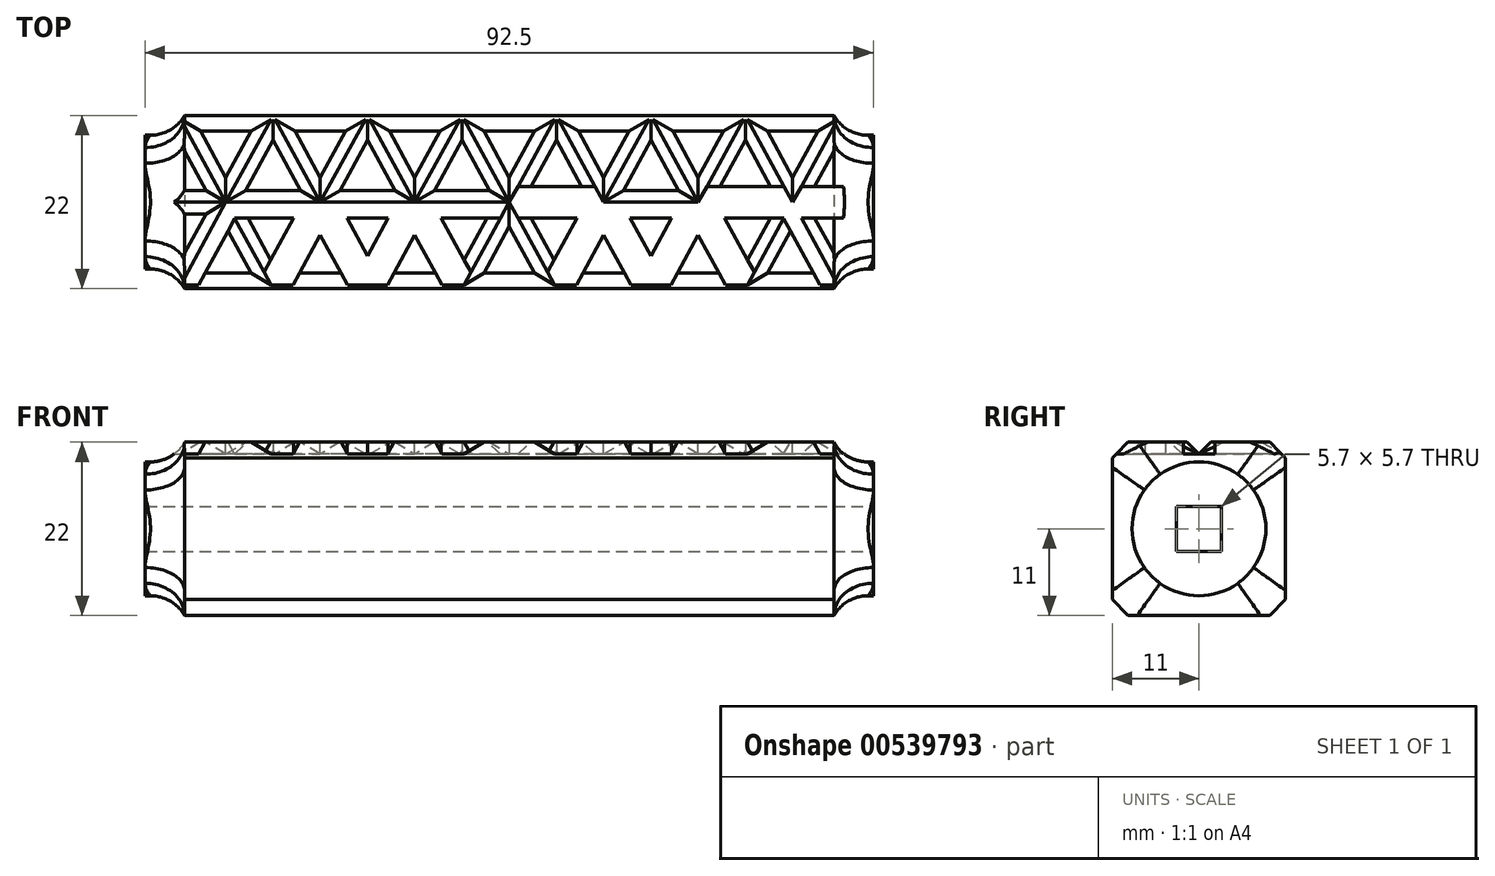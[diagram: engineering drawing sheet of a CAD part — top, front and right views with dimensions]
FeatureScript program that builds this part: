
annotation { "Feature Type Name" : "Feature", "Feature Type Description" : "" }
export const myFeature = defineFeature(function(context is Context, id is Id, definition is map)
    precondition{}
    {
        {
            var Q0;
            Q0=qCreatedBy(makeId("Top.planeOp"),FACE);
            var sketch = newSketch(context, id + "F0", { "sketchPlane" : qUnion([Q0])});
            skLineSegment(sketch, "E0.bottom", {"start": v(-46.25, 11) * mm, "end": v(46.25, 11) * mm});
            skLineSegment(sketch, "E0.top", {"start": v(-46.25, -11) * mm, "end": v(46.25, -11) * mm});
            skLineSegment(sketch, "E0.left", {"start": v(-46.25, 11) * mm, "end": v(-46.25, -11) * mm});
            skLineSegment(sketch, "E0.right", {"start": v(46.25, 11) * mm, "end": v(46.25, -11) * mm});
            skLineSegment(sketch, "E1", {"start": v(56.61, 0) * mm, "end": v(-55.2, 0) * mm});
            skPoint(sketch, "E1.endSnap0", {"position": v(-46.25, 0) * mm});
            skSolve(sketch);
        }
        {
            var Q0;
            Q0 = qSketchRegion(id + "F0", true);
            extrude(context, id + "F1", {"entities" : qUnion([Q0]), "endBound" : BoundingType.SYMMETRIC, "depth" : 22 * mm, "offsetDistance" : 25 * mm});
        }
        {
            var Q0;
            Q0=makeQuery(id+"F1.opExtrude","SWEPT_FACE",FACE,{"disambiguationData":[OSD([sQuery(id+"F0.wireOp",EDGE,"E0.right")])]});
            var sketch = newSketch(context, id + "F2", { "sketchPlane" : qUnion([Q0])});
            skLineSegment(sketch, "E2.bottom", {"start": v(2.85, 2.85) * mm, "end": v(-2.85, 2.85) * mm});
            skLineSegment(sketch, "E2.top", {"start": v(2.85, -2.85) * mm, "end": v(-2.85, -2.85) * mm});
            skLineSegment(sketch, "E2.left", {"start": v(2.85, 2.85) * mm, "end": v(2.85, -2.85) * mm});
            skLineSegment(sketch, "E2.right", {"start": v(-2.85, 2.85) * mm, "end": v(-2.85, -2.85) * mm});
            skSolve(sketch);
        }
        {
            var Q0;
            Q0=makeQuery(id+"F2.imprint","IMPRINT",FACE,{"disambiguationData":[TD([[makeQuery(id+"F2.imprint","IMPRINT",EDGE,{"derivedFrom":sQuery(id+"F2.wireOp",EDGE,"E2.bottom")}),1.0]])]});
            extrude(context, id + "F3", {"entities" : qUnion([Q0]), "operationType" : NewBodyOperationType.REMOVE, "oppositeDirection" : true, "depth" : 144.1 * mm, "offsetDistance" : 25 * mm});
        }
        {
            var Q0;
            Q0=makeQuery(id+"F1.opExtrude","SWEPT_FACE",FACE,{"disambiguationData":[OSD([sQuery(id+"F0.wireOp",EDGE,"E0.right")])]});
            var sketch = newSketch(context, id + "F4", { "sketchPlane" : qUnion([Q0])});
            skCircle(sketch, "E3", {"center": v(0, 0) * mm, "radius": 8.5 * mm});
            skSolve(sketch);
        }
        {
            var Q0;
            Q0=makeQuery(id+"F4.imprint","IMPRINT",FACE,{"disambiguationData":[TD([[makeQuery(id+"F4.imprint","IMPRINT",EDGE,{"derivedFrom":sQuery(id+"F4.wireOp",EDGE,"E3")}),-1.0]])]});
            extrude(context, id + "F5", {"entities" : qUnion([Q0]), "operationType" : NewBodyOperationType.REMOVE, "oppositeDirection" : true, "depth" : 5 * mm, "offsetDistance" : 25 * mm});
        }
        {
            var Q0;
            Q0=makeQuery(id+"F5.boolean.opBoolean","COPY",EDGE,{"derivedFrom":makeQuery(id+"F5.opExtrude","CAP_EDGE",EDGE,{"disambiguationData":[OSD([sQuery(id+"F4.wireOp",EDGE,"E3")])],"isStart":false})});
            fillet(context, id + "F6", {"entities" : qUnion([Q0]), "radius" : 5 * mm, "tangentPropagation" : true, "allowEdgeOverflow" : false});
        }
        {
            var Q0;
            Q0=makeQuery(id+"F1.opExtrude","SWEPT_FACE",FACE,{"disambiguationData":[OSD([sQuery(id+"F0.wireOp",EDGE,"E0.left")])]});
            var sketch = newSketch(context, id + "F7", { "sketchPlane" : qUnion([Q0])});
            skCircle(sketch, "E4", {"center": v(0, 0) * mm, "radius": 8.5 * mm});
            skSolve(sketch);
        }
        {
            var Q0;
            Q0=makeQuery(id+"F7.imprint","IMPRINT",FACE,{"disambiguationData":[TD([[makeQuery(id+"F7.imprint","IMPRINT",EDGE,{"derivedFrom":sQuery(id+"F7.wireOp",EDGE,"E4")}),-1.0]])]});
            extrude(context, id + "F8", {"entities" : qUnion([Q0]), "operationType" : NewBodyOperationType.REMOVE, "oppositeDirection" : true, "depth" : 5 * mm, "offsetDistance" : 25 * mm});
        }
        {
            var Q0;
            Q0=makeQuery(id+"F8.boolean.opBoolean","COPY",EDGE,{"derivedFrom":makeQuery(id+"F8.opExtrude","CAP_EDGE",EDGE,{"disambiguationData":[OSD([sQuery(id+"F7.wireOp",EDGE,"E4")])],"isStart":false})});
            fillet(context, id + "F9", {"entities" : qUnion([Q0]), "radius" : 5 * mm, "tangentPropagation" : true, "allowEdgeOverflow" : false});
        }
        {
            var Q0;
            Q0=makeQuery(id+"F1.opExtrude","CAP_FACE",FACE,{"disambiguationData":[OSD([sQuery(id+"F0.wireOp",EDGE,"E0.bottom"),sQuery(id+"F0.wireOp",EDGE,"E0.top"),sQuery(id+"F0.wireOp",EDGE,"E0.left"),sQuery(id+"F0.wireOp",EDGE,"E0.right")])],"isStart":false});
            var sketch = newSketch(context, id + "F10", { "sketchPlane" : qUnion([Q0])});
            skPoint(sketch, "E5.start.orphan", {"position": v(-41.25, 0) * mm});
            skLineSegment(sketch, "E6", {"start": v(-41.25, 2) * mm, "end": v(-39.37, 2) * mm});
            skLineSegment(sketch, "E7", {"start": v(-41.25, -2) * mm, "end": v(-39.37, -2) * mm});
            skLineSegment(sketch, "E8", {"start": v(-41.25, 2) * mm, "end": v(-47.22, 2) * mm});
            skLineSegment(sketch, "E9", {"start": v(-47.22, 2) * mm, "end": v(-47.22, -2) * mm});
            skLineSegment(sketch, "E10", {"start": v(-47.22, -2) * mm, "end": v(-41.25, -2) * mm});
            skLineSegment(sketch, "E11", {"start": v(41.25, 2) * mm, "end": v(49.02, 2) * mm});
            skLineSegment(sketch, "E12", {"start": v(49.02, 2) * mm, "end": v(49.02, -2) * mm});
            skLineSegment(sketch, "E13", {"start": v(49.02, -2) * mm, "end": v(41.25, -2) * mm});
            skLineSegment(sketch, "E14", {"start": v(-3.72, 11) * mm, "end": v(0, 4.18) * mm});
            skLineSegment(sketch, "E15", {"start": v(-6, 6.82) * mm, "end": v(-3.37, 2) * mm});
            skLineSegment(sketch, "E16", {"start": v(-8.28, 11) * mm, "end": v(-12, 4.18) * mm});
            skLineSegment(sketch, "E17", {"start": v(-15.72, 11) * mm, "end": v(-12, 4.18) * mm});
            skLineSegment(sketch, "E18", {"start": v(-18, 6.82) * mm, "end": v(-15.37, 2) * mm});
            skLineSegment(sketch, "E19.MirrorCS", {"start": v(-29.7, 2.09) * mm, "end": v(-29.65, 2) * mm});
            skLineSegment(sketch, "E20.MirrorCS", {"start": v(-29.7, 2.09) * mm, "end": v(-29.74, 2) * mm});
            skLineSegment(sketch, "E21.MirrorCS", {"start": v(-27.47, 2) * mm, "end": v(-27.42, 2.09) * mm});
            skLineSegment(sketch, "E22.MirrorCS", {"start": v(-27.42, 2.09) * mm, "end": v(-27.37, 2) * mm});
            skPoint(sketch, "E23.orphan", {"position": v(-20.28, 11) * mm});
            skPoint(sketch, "E24.orphan", {"position": v(-22.56, 11) * mm});
            skPoint(sketch, "E25.orphan", {"position": v(-24.83, 11) * mm});
            skPoint(sketch, "E26.orphan", {"position": v(-32.28, 11) * mm});
            skPoint(sketch, "E27.MirrorCS.start.orphan", {"position": v(-36.83, 11) * mm});
            skPoint(sketch, "E28.trimOffspring.end.orphan", {"position": v(-34.56, 11) * mm});
            skPoint(sketch, "E29.orphan", {"position": v(-32.28, -11) * mm});
            skPoint(sketch, "E30.orphan", {"position": v(-36.83, -11) * mm});
            skPoint(sketch, "E31.orphan", {"position": v(-20.28, -11) * mm});
            skPoint(sketch, "E32.orphan", {"position": v(-24.83, -11) * mm});
            skLineSegment(sketch, "E33", {"start": v(-18, -6.82) * mm, "end": v(-20.63, -2) * mm});
            skLineSegment(sketch, "E34", {"start": v(-20.28, -11) * mm, "end": v(-24, -4.18) * mm});
            skLineSegment(sketch, "E35", {"start": v(-32.28, 11) * mm, "end": v(-36, 4.18) * mm});
            skLineSegment(sketch, "E36", {"start": v(-20.28, 11) * mm, "end": v(-24, 4.18) * mm});
            skPoint(sketch, "E37.orphan", {"position": v(-6, 11) * mm});
            skLineSegment(sketch, "E38.trimOffspring", {"start": v(-6, 6.82) * mm, "end": v(-8.63, 2) * mm});
            skLineSegment(sketch, "E39.trimOffspring", {"start": v(-8.63, 2) * mm, "end": v(-3.37, 2) * mm});
            skLineSegment(sketch, "E40.trimOffspring", {"start": v(-8.63, -2) * mm, "end": v(-6, -6.82) * mm});
            skLineSegment(sketch, "E41.trimOffspring", {"start": v(-18, 6.82) * mm, "end": v(-20.63, 2) * mm});
            skPoint(sketch, "E42.trimOffspring.end.orphan", {"position": v(-18, 11) * mm});
            skLineSegment(sketch, "E43.trimOffspring", {"start": v(-24, 4.18) * mm, "end": v(-27.72, 11) * mm});
            skLineSegment(sketch, "E44.trimOffspring", {"start": v(-30, 6.82) * mm, "end": v(-32.63, 2) * mm});
            skLineSegment(sketch, "E45.trimOffspring", {"start": v(-20.63, 2) * mm, "end": v(-15.37, 2) * mm});
            skLineSegment(sketch, "E46.trimOffspring", {"start": v(-15.37, -2) * mm, "end": v(-18, -6.82) * mm});
            skLineSegment(sketch, "E47.trimOffspring", {"start": v(3.37, 2) * mm, "end": v(8.63, 2) * mm});
            skLineSegment(sketch, "E48.trimOffspring", {"start": v(-27.37, 2) * mm, "end": v(-30, 6.82) * mm});
            skLineSegment(sketch, "E49", {"start": v(-39.37, 2) * mm, "end": v(-41.25, 5.45) * mm});
            skPoint(sketch, "E50.orphan", {"position": v(-30, 11) * mm});
            skLineSegment(sketch, "E51.trimOffspring", {"start": v(-36, 4.18) * mm, "end": v(-39.72, 11) * mm});
            skPoint(sketch, "E52.orphan", {"position": v(-42, 11) * mm});
            skLineSegment(sketch, "E53.trimOffspring", {"start": v(-39.37, -2) * mm, "end": v(-41.25, -5.45) * mm});
            skLineSegment(sketch, "E54.trimOffspring", {"start": v(-32.63, 2) * mm, "end": v(-27.37, 2) * mm});
            skLineSegment(sketch, "E55.trimOffspring", {"start": v(-27.37, -2) * mm, "end": v(-30, -6.82) * mm});
            skLineSegment(sketch, "E56.MirrorCS", {"start": v(-27.47, -2) * mm, "end": v(-27.42, -2.09) * mm});
            skLineSegment(sketch, "E57.MirrorCS", {"start": v(-27.42, -2.09) * mm, "end": v(-27.37, -2) * mm});
            skLineSegment(sketch, "E58.MirrorCS", {"start": v(-29.7, -2.09) * mm, "end": v(-29.65, -2) * mm});
            skLineSegment(sketch, "E59.MirrorCS", {"start": v(-29.7, -2.09) * mm, "end": v(-29.74, -2) * mm});
            skLineSegment(sketch, "E60.MirrorCS", {"start": v(-6, -6.82) * mm, "end": v(-8.63, -2) * mm});
            skPoint(sketch, "E61.MirrorP", {"position": v(-18, -11) * mm});
            skLineSegment(sketch, "E62.MirrorCS", {"start": v(-32.28, -11) * mm, "end": v(-36, -4.18) * mm});
            skLineSegment(sketch, "E63.MirrorCS", {"start": v(-8.63, -2) * mm, "end": v(-3.37, -2) * mm});
            skLineSegment(sketch, "E64.MirrorCS", {"start": v(-8.28, -11) * mm, "end": v(-12, -4.18) * mm});
            skPoint(sketch, "E65.MirrorP", {"position": v(-22.56, -11) * mm});
            skLineSegment(sketch, "E66.MirrorCS", {"start": v(-18, -6.82) * mm, "end": v(-15.37, -2) * mm});
            skLineSegment(sketch, "E67.MirrorCS", {"start": v(-6, -6.82) * mm, "end": v(-3.37, -2) * mm});
            skPoint(sketch, "E68.MirrorP", {"position": v(-30, -11) * mm});
            skLineSegment(sketch, "E69.MirrorCS", {"start": v(-20.63, -2) * mm, "end": v(-15.37, -2) * mm});
            skLineSegment(sketch, "E70.MirrorCS", {"start": v(-32.63, -2) * mm, "end": v(-27.37, -2) * mm});
            skPoint(sketch, "E71.MirrorP", {"position": v(-34.56, -11) * mm});
            skLineSegment(sketch, "E72.MirrorCS", {"start": v(-30, -6.82) * mm, "end": v(-32.63, -2) * mm});
            skLineSegment(sketch, "E73.MirrorCS", {"start": v(-24, -4.18) * mm, "end": v(-27.72, -11) * mm});
            skLineSegment(sketch, "E74.MirrorCS", {"start": v(-15.72, -11) * mm, "end": v(-12, -4.18) * mm});
            skPoint(sketch, "E75.MirrorP", {"position": v(-42, -11) * mm});
            skLineSegment(sketch, "E76.MirrorCS", {"start": v(-36, -4.18) * mm, "end": v(-39.72, -11) * mm});
            skPoint(sketch, "E77.MirrorP", {"position": v(-6, -11) * mm});
            skLineSegment(sketch, "E78.trimOffspring", {"start": v(-34.9, -2) * mm, "end": v(-27.37, -2) * mm});
            skLineSegment(sketch, "E79.trimOffspring", {"start": v(-25.19, -2) * mm, "end": v(8.63, -2) * mm});
            skLineSegment(sketch, "E80.trimOffspring", {"start": v(-12, -4.18) * mm, "end": v(-8.28, -11) * mm});
            skLineSegment(sketch, "E81.trimOffspring", {"start": v(-12, -4.18) * mm, "end": v(-15.72, -11) * mm});
            skLineSegment(sketch, "E82", {"start": v(-3.72, -11) * mm, "end": v(0, -4.18) * mm});
            skPoint(sketch, "E83.orphan", {"position": v(8.28, -11) * mm});
            skLineSegment(sketch, "E84", {"start": v(-41.25, 5.45) * mm, "end": v(-44.21, 10.88) * mm});
            skLineSegment(sketch, "E85", {"start": v(-44.21, 10.88) * mm, "end": v(-40.6, 12.85) * mm});
            skLineSegment(sketch, "E86", {"start": v(-40.6, 12.85) * mm, "end": v(-39.52, 10.63) * mm});
            skLineSegment(sketch, "E87", {"start": v(-41.25, -5.45) * mm, "end": v(-44.22, -10.9) * mm});
            skLineSegment(sketch, "E88", {"start": v(-39.72, -11) * mm, "end": v(-41.25, -13.8) * mm});
            skLineSegment(sketch, "E89", {"start": v(-41.25, -13.8) * mm, "end": v(-44.22, -10.9) * mm});
            skLineSegment(sketch, "E90", {"start": v(-32.28, 11) * mm, "end": v(-27.72, 11) * mm});
            skLineSegment(sketch, "E91", {"start": v(-20.28, 11) * mm, "end": v(-15.72, 11) * mm});
            skLineSegment(sketch, "E92", {"start": v(-8.28, 11) * mm, "end": v(-3.72, 11) * mm});
            skLineSegment(sketch, "E93", {"start": v(-8.28, -11) * mm, "end": v(-3.72, -11) * mm});
            skLineSegment(sketch, "E94", {"start": v(-15.72, -11) * mm, "end": v(-20.28, -11) * mm});
            skLineSegment(sketch, "E95", {"start": v(-27.72, -11) * mm, "end": v(-32.28, -11) * mm});
            skLineSegment(sketch, "E96.MirrorCS", {"start": v(27.47, -2) * mm, "end": v(27.42, -2.09) * mm});
            skLineSegment(sketch, "E97.MirrorCS", {"start": v(27.42, -2.09) * mm, "end": v(27.37, -2) * mm});
            skLineSegment(sketch, "E98.MirrorCS", {"start": v(27.47, 2) * mm, "end": v(27.42, 2.09) * mm});
            skLineSegment(sketch, "E99.MirrorCS", {"start": v(27.42, 2.09) * mm, "end": v(27.37, 2) * mm});
            skLineSegment(sketch, "E100.MirrorCS", {"start": v(29.7, 2.09) * mm, "end": v(29.65, 2) * mm});
            skLineSegment(sketch, "E101.MirrorCS", {"start": v(29.7, -2.09) * mm, "end": v(29.65, -2) * mm});
            skLineSegment(sketch, "E102.MirrorCS", {"start": v(29.7, -2.09) * mm, "end": v(29.74, -2) * mm});
            skLineSegment(sketch, "E103.MirrorCS", {"start": v(41.25, -2) * mm, "end": v(39.37, -2) * mm});
            skLineSegment(sketch, "E104.MirrorCS", {"start": v(29.7, 2.09) * mm, "end": v(29.74, 2) * mm});
            skLineSegment(sketch, "E105.MirrorCS", {"start": v(32.63, -2) * mm, "end": v(27.37, -2) * mm});
            skLineSegment(sketch, "E106.MirrorCS", {"start": v(44.21, 10.88) * mm, "end": v(40.6, 12.85) * mm});
            skLineSegment(sketch, "E107.MirrorCS", {"start": v(41.25, 2) * mm, "end": v(39.37, 2) * mm});
            skPoint(sketch, "E108.MirrorP", {"position": v(22.56, -11) * mm});
            skLineSegment(sketch, "E109.MirrorCS", {"start": v(40.6, 12.85) * mm, "end": v(39.52, 10.63) * mm});
            skLineSegment(sketch, "E110.MirrorCS", {"start": v(41.25, -13.8) * mm, "end": v(44.22, -10.9) * mm});
            skLineSegment(sketch, "E111.MirrorCS", {"start": v(39.37, 2) * mm, "end": v(41.25, 5.45) * mm});
            skLineSegment(sketch, "E112.MirrorCS", {"start": v(32.63, 2) * mm, "end": v(27.37, 2) * mm});
            skLineSegment(sketch, "E113.MirrorCS", {"start": v(39.37, -2) * mm, "end": v(41.25, -5.45) * mm});
            skLineSegment(sketch, "E114.MirrorCS", {"start": v(39.72, -11) * mm, "end": v(41.25, -13.8) * mm});
            skLineSegment(sketch, "E115.MirrorCS", {"start": v(15.37, -2) * mm, "end": v(18, -6.82) * mm});
            skLineSegment(sketch, "E116.MirrorCS", {"start": v(24, -4.18) * mm, "end": v(27.72, -11) * mm});
            skLineSegment(sketch, "E117.MirrorCS", {"start": v(47.22, 2) * mm, "end": v(47.22, -2) * mm});
            skLineSegment(sketch, "E118.MirrorCS", {"start": v(18, -6.82) * mm, "end": v(20.63, -2) * mm});
            skPoint(sketch, "E119.MirrorP", {"position": v(20.28, -11) * mm});
            skLineSegment(sketch, "E120.MirrorCS", {"start": v(8.28, -11) * mm, "end": v(12, -4.18) * mm});
            skPoint(sketch, "E121.MirrorP", {"position": v(24.83, -11) * mm});
            skLineSegment(sketch, "E122.MirrorCS", {"start": v(20.63, -2) * mm, "end": v(15.37, -2) * mm});
            skLineSegment(sketch, "E123.MirrorCS", {"start": v(20.28, 11) * mm, "end": v(15.72, 11) * mm});
            skLineSegment(sketch, "E124.MirrorCS", {"start": v(36, -4.18) * mm, "end": v(39.72, -11) * mm});
            skLineSegment(sketch, "E125.MirrorCS", {"start": v(27.72, -11) * mm, "end": v(32.28, -11) * mm});
            skPoint(sketch, "E126.MirrorP", {"position": v(32.28, -11) * mm});
            skLineSegment(sketch, "E127.MirrorCS", {"start": v(8.28, -11) * mm, "end": v(3.72, -11) * mm});
            skLineSegment(sketch, "E128.MirrorCS", {"start": v(15.72, -11) * mm, "end": v(20.28, -11) * mm});
            skPoint(sketch, "E129.MirrorP", {"position": v(36.83, -11) * mm});
            skPoint(sketch, "E130.MirrorP", {"position": v(34.56, -11) * mm});
            skLineSegment(sketch, "E131.MirrorCS", {"start": v(8.63, -2) * mm, "end": v(6, -6.82) * mm});
            skLineSegment(sketch, "E132.MirrorCS", {"start": v(32.28, 11) * mm, "end": v(27.72, 11) * mm});
            skLineSegment(sketch, "E133.MirrorCS", {"start": v(15.72, -11) * mm, "end": v(12, -4.18) * mm});
            skLineSegment(sketch, "E134.MirrorCS", {"start": v(20.28, -11) * mm, "end": v(24, -4.18) * mm});
            skLineSegment(sketch, "E135.MirrorCS", {"start": v(27.37, -2) * mm, "end": v(30, -6.82) * mm});
            skLineSegment(sketch, "E136.MirrorCS", {"start": v(8.28, 11) * mm, "end": v(3.72, 11) * mm});
            skPoint(sketch, "E137.MirrorP", {"position": v(6, 11) * mm});
            skLineSegment(sketch, "E138.MirrorCS", {"start": v(41.25, 5.45) * mm, "end": v(44.21, 10.88) * mm});
            skLineSegment(sketch, "E139.MirrorCS", {"start": v(41.25, -5.45) * mm, "end": v(44.22, -10.9) * mm});
            skLineSegment(sketch, "E140.MirrorCS", {"start": v(30, -6.82) * mm, "end": v(32.63, -2) * mm});
            skLineSegment(sketch, "E141.MirrorCS", {"start": v(8.63, -2) * mm, "end": v(3.37, -2) * mm});
            skLineSegment(sketch, "E142.MirrorCS", {"start": v(18, 6.82) * mm, "end": v(15.37, 2) * mm});
            skPoint(sketch, "E143.MirrorP", {"position": v(6, -11) * mm});
            skPoint(sketch, "E144.MirrorP", {"position": v(18, 11) * mm});
            skLineSegment(sketch, "E145.MirrorCS", {"start": v(8.63, 2) * mm, "end": v(3.37, 2) * mm});
            skLineSegment(sketch, "E146.MirrorCS", {"start": v(8.28, 11) * mm, "end": v(12, 4.18) * mm});
            skPoint(sketch, "E147.MirrorP", {"position": v(20.28, 11) * mm});
            skPoint(sketch, "E148.MirrorP", {"position": v(22.56, 11) * mm});
            skPoint(sketch, "E149.MirrorP", {"position": v(42, 11) * mm});
            skLineSegment(sketch, "E150.MirrorCS", {"start": v(18, 6.82) * mm, "end": v(20.63, 2) * mm});
            skLineSegment(sketch, "E151.MirrorCS", {"start": v(24, 4.18) * mm, "end": v(27.72, 11) * mm});
            skLineSegment(sketch, "E152.MirrorCS", {"start": v(6, -6.82) * mm, "end": v(8.63, -2) * mm});
            skPoint(sketch, "E153.MirrorP", {"position": v(36.83, 11) * mm});
            skPoint(sketch, "E154.MirrorP", {"position": v(34.56, 11) * mm});
            skPoint(sketch, "E155.MirrorP", {"position": v(18, -11) * mm});
            skLineSegment(sketch, "E156.MirrorCS", {"start": v(15.72, 11) * mm, "end": v(12, 4.18) * mm});
            skLineSegment(sketch, "E157.MirrorCS", {"start": v(32.28, 11) * mm, "end": v(36, 4.18) * mm});
            skLineSegment(sketch, "E158.MirrorCS", {"start": v(12, -4.18) * mm, "end": v(15.72, -11) * mm});
            skPoint(sketch, "E159.MirrorP", {"position": v(42, -11) * mm});
            skLineSegment(sketch, "E160.MirrorCS", {"start": v(36, 4.18) * mm, "end": v(39.72, 11) * mm});
            skPoint(sketch, "E161.MirrorP", {"position": v(30, 11) * mm});
            skPoint(sketch, "E162.MirrorP", {"position": v(30, -11) * mm});
            skPoint(sketch, "E163.MirrorP", {"position": v(24.83, 11) * mm});
            skPoint(sketch, "E164.MirrorP", {"position": v(32.28, 11) * mm});
            skLineSegment(sketch, "E165.MirrorCS", {"start": v(20.63, 2) * mm, "end": v(15.37, 2) * mm});
            skLineSegment(sketch, "E166.MirrorCS", {"start": v(3.72, 11) * mm, "end": v(0, 4.18) * mm});
            skLineSegment(sketch, "E167.MirrorCS", {"start": v(27.37, 2) * mm, "end": v(30, 6.82) * mm});
            skLineSegment(sketch, "E168.MirrorCS", {"start": v(6, -6.82) * mm, "end": v(3.37, -2) * mm});
            skLineSegment(sketch, "E169.MirrorCS", {"start": v(30, 6.82) * mm, "end": v(32.63, 2) * mm});
            skLineSegment(sketch, "E170.MirrorCS", {"start": v(32.28, -11) * mm, "end": v(36, -4.18) * mm});
            skLineSegment(sketch, "E171.MirrorCS", {"start": v(3.72, -11) * mm, "end": v(0, -4.18) * mm});
            skLineSegment(sketch, "E172.MirrorCS", {"start": v(6, 6.82) * mm, "end": v(3.37, 2) * mm});
            skLineSegment(sketch, "E173.MirrorCS", {"start": v(12, -4.18) * mm, "end": v(8.28, -11) * mm});
            skLineSegment(sketch, "E174.MirrorCS", {"start": v(20.28, 11) * mm, "end": v(24, 4.18) * mm});
            skLineSegment(sketch, "E175.MirrorCS", {"start": v(41.25, 2) * mm, "end": v(47.22, 2) * mm});
            skLineSegment(sketch, "E176.MirrorCS", {"start": v(18, -6.82) * mm, "end": v(15.37, -2) * mm});
            skLineSegment(sketch, "E177.MirrorCS", {"start": v(6, 6.82) * mm, "end": v(8.63, 2) * mm});
            skLineSegment(sketch, "E178.MirrorCS", {"start": v(47.22, -2) * mm, "end": v(41.25, -2) * mm});
            skPoint(sketch, "E179.orphan", {"position": v(-3.37, -2) * mm});
            skPoint(sketch, "E180.orphan", {"position": v(3.37, -2) * mm});
            skLineSegment(sketch, "E181.trimOffspring", {"start": v(8.63, -2) * mm, "end": v(-41.25, -2) * mm});
            skLineSegment(sketch, "E182.trimOffspring", {"start": v(15.37, -2) * mm, "end": v(20.63, -2) * mm});
            skLineSegment(sketch, "E183.trimOffspring", {"start": v(27.37, 2) * mm, "end": v(32.63, 2) * mm});
            skLineSegment(sketch, "E184.trimOffspring", {"start": v(27.37, -2) * mm, "end": v(32.63, -2) * mm});
            skLineSegment(sketch, "E185.trimOffspring", {"start": v(39.37, -2) * mm, "end": v(41.25, -2) * mm});
            skLineSegment(sketch, "E186.trimOffspring", {"start": v(39.37, 2) * mm, "end": v(41.25, 2) * mm});
            skSolve(sketch);
        }
        {
            var Q0;
            Q0=makeQuery(id+"F1.opExtrude","CAP_EDGE",EDGE,{"disambiguationData":[OSD([sQuery(id+"F0.wireOp",EDGE,"E0.top")])],"isStart":false});
            var Q1;
            Q1=makeQuery(id+"F1.opExtrude","CAP_EDGE",EDGE,{"disambiguationData":[OSD([sQuery(id+"F0.wireOp",EDGE,"E0.bottom")])],"isStart":false});
            var Q2;
            Q2=makeQuery(id+"F1.opExtrude","CAP_EDGE",EDGE,{"disambiguationData":[OSD([sQuery(id+"F0.wireOp",EDGE,"E0.bottom")])],"isStart":true});
            var Q3;
            Q3=makeQuery(id+"F1.opExtrude","CAP_EDGE",EDGE,{"disambiguationData":[OSD([sQuery(id+"F0.wireOp",EDGE,"E0.top")])],"isStart":true});
            chamfer(context, id + "F11", {"entities" : qUnion([Q0, Q1, Q2, Q3]), "width" : 2 * mm, "tangentPropagation" : true});
        }
        {
            var Q0;
            Q0=makeQuery(id+"F10.imprint","IMPRINT",FACE,{"disambiguationData":[TD([[makeQuery(id+"F10.imprint","IMPRINT",EDGE,{"derivedFrom":sQuery(id+"F10.wireOp",EDGE,"E6")}),-1.0]])]});
            var Q1;
            {var subQ0=sQuery(id+"F10.wireOp",EDGE,"E11");Q1=makeQuery(id+"F10.imprint","IMPRINT",FACE,{"disambiguationData":[TD([[makeQuery(id+"F10.imprint","IMPRINT",EDGE,{"derivedFrom":subQ0}),-1.0]])]});}
            var Q2;
            {var subQ0=sQuery(id+"F10.wireOp",EDGE,"E8");Q2=makeQuery(id+"F10.imprint","IMPRINT",FACE,{"disambiguationData":[TD([[makeQuery(id+"F10.imprint","IMPRINT",EDGE,{"derivedFrom":subQ0}),1.0]])]});}
            var Q3;
            {var subQ12=sQuery(id+"F10.wireOp",EDGE,"E53.trimOffspring");Q3=makeQuery(id+"F10.imprint","IMPRINT",FACE,{"disambiguationData":[TD([[makeQuery(id+"F10.imprint","IMPRINT",EDGE,{"derivedFrom":subQ12}),1.0]])]});}
            var Q4;
            Q4=makeQuery(id+"F10.imprint","IMPRINT",FACE,{"disambiguationData":[TD([[makeQuery(id+"F10.imprint","IMPRINT",EDGE,{"derivedFrom":sQuery(id+"F10.wireOp",EDGE,"E117.MirrorCS")}),-1.0]])]});
            var Q5;
            Q5=makeQuery(id+"F10.imprint","IMPRINT",FACE,{"disambiguationData":[TD([[makeQuery(id+"F10.imprint","IMPRINT",EDGE,{"derivedFrom":sQuery(id+"F10.wireOp",EDGE,"E110.MirrorCS")}),1.0]])]});
            var Q6;
            {var subQ4=sQuery(id+"F10.wireOp",EDGE,"E106.MirrorCS");Q6=makeQuery(id+"F10.imprint","IMPRINT",FACE,{"disambiguationData":[TD([[makeQuery(id+"F10.imprint","IMPRINT",EDGE,{"derivedFrom":subQ4}),1.0]])]});}
            var Q7;
            {var subQ7=sQuery(id+"F10.wireOp",EDGE,"E84");Q7=makeQuery(id+"F10.imprint","IMPRINT",FACE,{"disambiguationData":[TD([[makeQuery(id+"F10.imprint","IMPRINT",EDGE,{"derivedFrom":subQ7}),-1.0]])]});}
            var Q8;
            {var subQ5=sQuery(id+"F10.wireOp",EDGE,"E87");Q8=makeQuery(id+"F10.imprint","IMPRINT",FACE,{"disambiguationData":[TD([[makeQuery(id+"F10.imprint","IMPRINT",EDGE,{"derivedFrom":subQ5}),1.0]])]});}
            extrude(context, id + "F12", {"entities" : qUnion([Q0, Q1, Q2, Q3, Q4, Q5, Q6, Q7, Q8]), "operationType" : NewBodyOperationType.REMOVE, "oppositeDirection" : true, "depth" : 1.5 * mm, "offsetDistance" : 25 * mm});
        }
        {
            var Q0;
            Q0=makeQuery(id+"F12.boolean.opBoolean","COPY",EDGE,{"derivedFrom":makeQuery(id+"F12.opExtrude","CAP_EDGE",EDGE,{"disambiguationData":[OSD([sQuery(id+"F10.wireOp",EDGE,"E6")])],"isStart":false})});
            var Q1;
            Q1=makeQuery(id+"F12.boolean.opBoolean","COPY",EDGE,{"derivedFrom":makeQuery(id+"F12.opExtrude","CAP_EDGE",EDGE,{"disambiguationData":[OSD([sQuery(id+"F10.wireOp",EDGE,"E7"),sQuery(id+"F10.wireOp",EDGE,"E10"),sQuery(id+"F10.wireOp",EDGE,"E13")])],"isStart":false})});
            var Q2;
            Q2=makeQuery(id+"F12.boolean.opBoolean","COPY",EDGE,{"derivedFrom":makeQuery(id+"F12.opExtrude","CAP_EDGE",EDGE,{"disambiguationData":[OSD([sQuery(id+"F10.wireOp",EDGE,"E54.trimOffspring")])],"isStart":false})});
            var Q3;
            Q3=makeQuery(id+"F12.boolean.opBoolean","COPY",EDGE,{"derivedFrom":makeQuery(id+"F12.opExtrude","CAP_EDGE",EDGE,{"disambiguationData":[OSD([sQuery(id+"F10.wireOp",EDGE,"E44.trimOffspring")])],"isStart":false})});
            var Q4;
            Q4=makeQuery(id+"F12.boolean.opBoolean","COPY",EDGE,{"derivedFrom":makeQuery(id+"F12.opExtrude","CAP_EDGE",EDGE,{"disambiguationData":[OSD([sQuery(id+"F10.wireOp",EDGE,"E43.trimOffspring")])],"isStart":false})});
            var Q5;
            Q5=makeQuery(id+"F12.boolean.opBoolean","COPY",EDGE,{"derivedFrom":makeQuery(id+"F12.opExtrude","CAP_EDGE",EDGE,{"disambiguationData":[OSD([sQuery(id+"F10.wireOp",EDGE,"E48.trimOffspring")])],"isStart":false})});
            var Q6;
            Q6=makeQuery(id+"F12.boolean.opBoolean","COPY",EDGE,{"derivedFrom":makeQuery(id+"F12.opExtrude","CAP_EDGE",EDGE,{"disambiguationData":[OSD([sQuery(id+"F10.wireOp",EDGE,"E35")])],"isStart":false})});
            var Q7;
            Q7=makeQuery(id+"F12.boolean.opBoolean","COPY",EDGE,{"derivedFrom":makeQuery(id+"F12.opExtrude","CAP_EDGE",EDGE,{"disambiguationData":[OSD([sQuery(id+"F10.wireOp",EDGE,"E51.trimOffspring")])],"isStart":false})});
            var Q8;
            Q8=makeQuery(id+"F12.boolean.opBoolean","COPY",EDGE,{"derivedFrom":makeQuery(id+"F12.opExtrude","CAP_EDGE",EDGE,{"disambiguationData":[OSD([sQuery(id+"F10.wireOp",EDGE,"E49")])],"isStart":false})});
            var Q9;
            Q9=makeQuery(id+"F12.boolean.opBoolean","COPY",EDGE,{"derivedFrom":makeQuery(id+"F12.opExtrude","CAP_EDGE",EDGE,{"disambiguationData":[OSD([sQuery(id+"F10.wireOp",EDGE,"E10"),sQuery(id+"F10.wireOp",EDGE,"E181.trimOffspring")])],"isStart":false})});
            var Q10;
            {var subQ0=sQuery(id+"F10.wireOp",EDGE,"E181.trimOffspring");var subQ1=makeQuery(id+"F10.imprint","INTERSECT",VERTEX,{"derivedFrom":[sQuery(id+"F10.wireOp",EDGE,"E59.MirrorCS"),subQ0]});var subQ2=makeQuery(id+"F10.imprint","INTERSECT",VERTEX,{"derivedFrom":[sQuery(id+"F10.wireOp",EDGE,"E58.MirrorCS"),subQ0]});var subQ3=makeQuery(id+"F10.imprint","INTERSECT",VERTEX,{"derivedFrom":[sQuery(id+"F10.wireOp",EDGE,"E56.MirrorCS"),subQ0]});Q10=makeQuery(id+"F12.boolean.opBoolean","COPY",EDGE,{"derivedFrom":makeQuery(id+"F12.opExtrude","CAP_EDGE",EDGE,{"disambiguationData":[OSD([subQ0]),TDD([makeQuery(id+"F10.imprint","IMPRINT",EDGE,{"disambiguationData":[TD([[subQ3,1.0]])],"derivedFrom":subQ0}),makeQuery(id+"F10.imprint","IMPRINT",EDGE,{"disambiguationData":[TD([[subQ3,-1.0]])],"derivedFrom":subQ0}),makeQuery(id+"F10.imprint","IMPRINT",EDGE,{"disambiguationData":[TD([[subQ2,-1.0]])],"derivedFrom":subQ0}),makeQuery(id+"F10.imprint","IMPRINT",EDGE,{"disambiguationData":[TD([[subQ1,-1.0]])],"derivedFrom":subQ0})])],"isStart":false})});}
            var Q11;
            {var subQ0=sQuery(id+"F10.wireOp",EDGE,"E181.trimOffspring");Q11=makeQuery(id+"F12.boolean.opBoolean","COPY",EDGE,{"derivedFrom":makeQuery(id+"F12.opExtrude","CAP_EDGE",EDGE,{"disambiguationData":[OSD([subQ0]),TDD([makeQuery(id+"F10.imprint","IMPRINT",EDGE,{"disambiguationData":[TD([[makeQuery(id+"F10.imprint","INTERSECT",VERTEX,{"derivedFrom":[sQuery(id+"F10.wireOp",EDGE,"E66.MirrorCS"),subQ0]}),-1.0]])],"derivedFrom":subQ0})])],"isStart":false})});}
            var Q12;
            {var subQ0=sQuery(id+"F10.wireOp",EDGE,"E181.trimOffspring");Q12=makeQuery(id+"F12.boolean.opBoolean","COPY",EDGE,{"derivedFrom":makeQuery(id+"F12.opExtrude","CAP_EDGE",EDGE,{"disambiguationData":[OSD([subQ0]),TDD([makeQuery(id+"F10.imprint","IMPRINT",EDGE,{"disambiguationData":[TD([[makeQuery(id+"F10.imprint","INTERSECT",VERTEX,{"derivedFrom":[sQuery(id+"F10.wireOp",EDGE,"E60.MirrorCS"),subQ0]}),1.0]])],"derivedFrom":subQ0})])],"isStart":false})});}
            var Q13;
            {var subQ0=sQuery(id+"F10.wireOp",EDGE,"E181.trimOffspring");Q13=makeQuery(id+"F12.boolean.opBoolean","COPY",EDGE,{"derivedFrom":makeQuery(id+"F12.opExtrude","CAP_EDGE",EDGE,{"disambiguationData":[OSD([subQ0]),TDD([makeQuery(id+"F10.imprint","IMPRINT",EDGE,{"disambiguationData":[TD([[makeQuery(id+"F10.imprint","INTERSECT",VERTEX,{"derivedFrom":[sQuery(id+"F10.wireOp",EDGE,"E152.MirrorCS"),subQ0]}),-1.0]])],"derivedFrom":subQ0})])],"isStart":false})});}
            var Q14;
            Q14=makeQuery(id+"F12.boolean.opBoolean","COPY",EDGE,{"derivedFrom":makeQuery(id+"F12.opExtrude","CAP_EDGE",EDGE,{"disambiguationData":[OSD([sQuery(id+"F10.wireOp",EDGE,"E62.MirrorCS")])],"isStart":false})});
            var Q15;
            Q15=makeQuery(id+"F12.boolean.opBoolean","COPY",EDGE,{"derivedFrom":makeQuery(id+"F12.opExtrude","CAP_EDGE",EDGE,{"disambiguationData":[OSD([sQuery(id+"F10.wireOp",EDGE,"E34")])],"isStart":false})});
            var Q16;
            Q16=makeQuery(id+"F12.boolean.opBoolean","COPY",EDGE,{"derivedFrom":makeQuery(id+"F12.opExtrude","CAP_EDGE",EDGE,{"disambiguationData":[OSD([sQuery(id+"F10.wireOp",EDGE,"E80.trimOffspring")])],"isStart":false})});
            var Q17;
            Q17=makeQuery(id+"F12.boolean.opBoolean","COPY",EDGE,{"derivedFrom":makeQuery(id+"F12.opExtrude","CAP_EDGE",EDGE,{"disambiguationData":[OSD([sQuery(id+"F10.wireOp",EDGE,"E171.MirrorCS")])],"isStart":false})});
            var Q18;
            Q18=makeQuery(id+"F12.boolean.opBoolean","COPY",EDGE,{"derivedFrom":makeQuery(id+"F12.opExtrude","CAP_EDGE",EDGE,{"disambiguationData":[OSD([sQuery(id+"F10.wireOp",EDGE,"E18")])],"isStart":false})});
            var Q19;
            Q19=makeQuery(id+"F12.boolean.opBoolean","COPY",EDGE,{"derivedFrom":makeQuery(id+"F12.opExtrude","CAP_EDGE",EDGE,{"disambiguationData":[OSD([sQuery(id+"F10.wireOp",EDGE,"E41.trimOffspring")])],"isStart":false})});
            var Q20;
            Q20=makeQuery(id+"F12.boolean.opBoolean","COPY",EDGE,{"derivedFrom":makeQuery(id+"F12.opExtrude","CAP_EDGE",EDGE,{"disambiguationData":[OSD([sQuery(id+"F10.wireOp",EDGE,"E33")])],"isStart":false})});
            var Q21;
            Q21=makeQuery(id+"F12.boolean.opBoolean","COPY",EDGE,{"derivedFrom":makeQuery(id+"F12.opExtrude","CAP_EDGE",EDGE,{"disambiguationData":[OSD([sQuery(id+"F10.wireOp",EDGE,"E72.MirrorCS")])],"isStart":false})});
            var Q22;
            Q22=makeQuery(id+"F12.boolean.opBoolean","COPY",EDGE,{"derivedFrom":makeQuery(id+"F12.opExtrude","CAP_EDGE",EDGE,{"disambiguationData":[OSD([sQuery(id+"F10.wireOp",EDGE,"E76.MirrorCS")])],"isStart":false})});
            var Q23;
            Q23=makeQuery(id+"F12.boolean.opBoolean","COPY",EDGE,{"derivedFrom":makeQuery(id+"F12.opExtrude","CAP_EDGE",EDGE,{"disambiguationData":[OSD([sQuery(id+"F10.wireOp",EDGE,"E53.trimOffspring")])],"isStart":false})});
            var Q24;
            Q24=makeQuery(id+"F12.boolean.opBoolean","COPY",EDGE,{"derivedFrom":makeQuery(id+"F12.opExtrude","CAP_EDGE",EDGE,{"disambiguationData":[OSD([sQuery(id+"F10.wireOp",EDGE,"E73.MirrorCS")])],"isStart":false})});
            var Q25;
            Q25=makeQuery(id+"F12.boolean.opBoolean","COPY",EDGE,{"derivedFrom":makeQuery(id+"F12.opExtrude","CAP_EDGE",EDGE,{"disambiguationData":[OSD([sQuery(id+"F10.wireOp",EDGE,"E81.trimOffspring")])],"isStart":false})});
            var Q26;
            Q26=makeQuery(id+"F12.boolean.opBoolean","COPY",EDGE,{"derivedFrom":makeQuery(id+"F12.opExtrude","CAP_EDGE",EDGE,{"disambiguationData":[OSD([sQuery(id+"F10.wireOp",EDGE,"E82")])],"isStart":false})});
            var Q27;
            Q27=makeQuery(id+"F12.boolean.opBoolean","COPY",EDGE,{"derivedFrom":makeQuery(id+"F12.opExtrude","CAP_EDGE",EDGE,{"disambiguationData":[OSD([sQuery(id+"F10.wireOp",EDGE,"E173.MirrorCS")])],"isStart":false})});
            var Q28;
            Q28=makeQuery(id+"F12.boolean.opBoolean","COPY",EDGE,{"derivedFrom":makeQuery(id+"F12.opExtrude","CAP_EDGE",EDGE,{"disambiguationData":[OSD([sQuery(id+"F10.wireOp",EDGE,"E134.MirrorCS")])],"isStart":false})});
            var Q29;
            Q29=makeQuery(id+"F12.boolean.opBoolean","COPY",EDGE,{"derivedFrom":makeQuery(id+"F12.opExtrude","CAP_EDGE",EDGE,{"disambiguationData":[OSD([sQuery(id+"F10.wireOp",EDGE,"E168.MirrorCS")])],"isStart":false})});
            var Q30;
            Q30=makeQuery(id+"F12.boolean.opBoolean","COPY",EDGE,{"derivedFrom":makeQuery(id+"F12.opExtrude","CAP_EDGE",EDGE,{"disambiguationData":[OSD([sQuery(id+"F10.wireOp",EDGE,"E172.MirrorCS")])],"isStart":false})});
            var Q31;
            Q31=makeQuery(id+"F12.boolean.opBoolean","COPY",EDGE,{"derivedFrom":makeQuery(id+"F12.opExtrude","CAP_EDGE",EDGE,{"disambiguationData":[OSD([sQuery(id+"F10.wireOp",EDGE,"E14")])],"isStart":false})});
            var Q32;
            Q32=makeQuery(id+"F12.boolean.opBoolean","COPY",EDGE,{"derivedFrom":makeQuery(id+"F12.opExtrude","CAP_EDGE",EDGE,{"disambiguationData":[OSD([sQuery(id+"F10.wireOp",EDGE,"E36")])],"isStart":false})});
            var Q33;
            Q33=makeQuery(id+"F12.boolean.opBoolean","COPY",EDGE,{"derivedFrom":makeQuery(id+"F12.opExtrude","CAP_EDGE",EDGE,{"disambiguationData":[OSD([sQuery(id+"F10.wireOp",EDGE,"E66.MirrorCS")])],"isStart":false})});
            var Q34;
            Q34=makeQuery(id+"F12.boolean.opBoolean","COPY",EDGE,{"derivedFrom":makeQuery(id+"F12.opExtrude","CAP_EDGE",EDGE,{"disambiguationData":[OSD([sQuery(id+"F10.wireOp",EDGE,"E16")])],"isStart":false})});
            var Q35;
            Q35=makeQuery(id+"F12.boolean.opBoolean","COPY",EDGE,{"derivedFrom":makeQuery(id+"F12.opExtrude","CAP_EDGE",EDGE,{"disambiguationData":[OSD([sQuery(id+"F10.wireOp",EDGE,"E45.trimOffspring")])],"isStart":false})});
            var Q36;
            Q36=makeQuery(id+"F12.boolean.opBoolean","COPY",EDGE,{"derivedFrom":makeQuery(id+"F12.opExtrude","CAP_EDGE",EDGE,{"disambiguationData":[OSD([sQuery(id+"F10.wireOp",EDGE,"E39.trimOffspring")])],"isStart":false})});
            var Q37;
            Q37=makeQuery(id+"F12.boolean.opBoolean","COPY",EDGE,{"derivedFrom":makeQuery(id+"F12.opExtrude","CAP_EDGE",EDGE,{"disambiguationData":[OSD([sQuery(id+"F10.wireOp",EDGE,"E145.MirrorCS")])],"isStart":false})});
            var Q38;
            Q38=makeQuery(id+"F12.boolean.opBoolean","COPY",EDGE,{"derivedFrom":makeQuery(id+"F12.opExtrude","CAP_EDGE",EDGE,{"disambiguationData":[OSD([sQuery(id+"F10.wireOp",EDGE,"E165.MirrorCS")])],"isStart":false})});
            var Q39;
            Q39=makeQuery(id+"F12.boolean.opBoolean","COPY",EDGE,{"derivedFrom":makeQuery(id+"F12.opExtrude","CAP_EDGE",EDGE,{"disambiguationData":[OSD([sQuery(id+"F10.wireOp",EDGE,"E152.MirrorCS")])],"isStart":false})});
            var Q40;
            Q40=makeQuery(id+"F12.boolean.opBoolean","COPY",EDGE,{"derivedFrom":makeQuery(id+"F12.opExtrude","CAP_EDGE",EDGE,{"disambiguationData":[OSD([sQuery(id+"F10.wireOp",EDGE,"E67.MirrorCS")])],"isStart":false})});
            var Q41;
            Q41=makeQuery(id+"F12.boolean.opBoolean","COPY",EDGE,{"derivedFrom":makeQuery(id+"F12.opExtrude","CAP_EDGE",EDGE,{"disambiguationData":[OSD([sQuery(id+"F10.wireOp",EDGE,"E17")])],"isStart":false})});
            var Q42;
            Q42=makeQuery(id+"F12.boolean.opBoolean","COPY",EDGE,{"derivedFrom":makeQuery(id+"F12.opExtrude","CAP_EDGE",EDGE,{"disambiguationData":[OSD([sQuery(id+"F10.wireOp",EDGE,"E60.MirrorCS")])],"isStart":false})});
            var Q43;
            Q43=makeQuery(id+"F12.boolean.opBoolean","COPY",EDGE,{"derivedFrom":makeQuery(id+"F12.opExtrude","CAP_EDGE",EDGE,{"disambiguationData":[OSD([sQuery(id+"F10.wireOp",EDGE,"E166.MirrorCS")])],"isStart":false})});
            var Q44;
            Q44=makeQuery(id+"F12.boolean.opBoolean","COPY",EDGE,{"derivedFrom":makeQuery(id+"F12.opExtrude","CAP_EDGE",EDGE,{"disambiguationData":[OSD([sQuery(id+"F10.wireOp",EDGE,"E156.MirrorCS")])],"isStart":false})});
            var Q45;
            Q45=makeQuery(id+"F12.boolean.opBoolean","COPY",EDGE,{"derivedFrom":makeQuery(id+"F12.opExtrude","CAP_EDGE",EDGE,{"disambiguationData":[OSD([sQuery(id+"F10.wireOp",EDGE,"E55.trimOffspring")])],"isStart":false})});
            var Q46;
            Q46=makeQuery(id+"F12.boolean.opBoolean","COPY",EDGE,{"derivedFrom":makeQuery(id+"F12.opExtrude","CAP_EDGE",EDGE,{"disambiguationData":[OSD([sQuery(id+"F10.wireOp",EDGE,"E177.MirrorCS")])],"isStart":false})});
            var Q47;
            Q47=makeQuery(id+"F12.boolean.opBoolean","COPY",EDGE,{"derivedFrom":makeQuery(id+"F12.opExtrude","CAP_EDGE",EDGE,{"disambiguationData":[OSD([sQuery(id+"F10.wireOp",EDGE,"E150.MirrorCS")])],"isStart":false})});
            var Q48;
            Q48=makeQuery(id+"F12.boolean.opBoolean","COPY",EDGE,{"derivedFrom":makeQuery(id+"F12.opExtrude","CAP_EDGE",EDGE,{"disambiguationData":[OSD([sQuery(id+"F10.wireOp",EDGE,"E142.MirrorCS")])],"isStart":false})});
            var Q49;
            Q49=makeQuery(id+"F12.boolean.opBoolean","COPY",EDGE,{"derivedFrom":makeQuery(id+"F12.opExtrude","CAP_EDGE",EDGE,{"disambiguationData":[OSD([sQuery(id+"F10.wireOp",EDGE,"E146.MirrorCS")])],"isStart":false})});
            var Q50;
            Q50=makeQuery(id+"F12.boolean.opBoolean","COPY",EDGE,{"derivedFrom":makeQuery(id+"F12.opExtrude","CAP_EDGE",EDGE,{"disambiguationData":[OSD([sQuery(id+"F10.wireOp",EDGE,"E176.MirrorCS")])],"isStart":false})});
            var Q51;
            Q51=makeQuery(id+"F12.boolean.opBoolean","COPY",EDGE,{"derivedFrom":makeQuery(id+"F12.opExtrude","CAP_EDGE",EDGE,{"disambiguationData":[OSD([sQuery(id+"F10.wireOp",EDGE,"E174.MirrorCS")])],"isStart":false})});
            var Q52;
            Q52=makeQuery(id+"F12.boolean.opBoolean","COPY",EDGE,{"derivedFrom":makeQuery(id+"F12.opExtrude","CAP_EDGE",EDGE,{"disambiguationData":[OSD([sQuery(id+"F10.wireOp",EDGE,"E151.MirrorCS")])],"isStart":false})});
            var Q53;
            Q53=makeQuery(id+"F12.boolean.opBoolean","COPY",EDGE,{"derivedFrom":makeQuery(id+"F12.opExtrude","CAP_EDGE",EDGE,{"disambiguationData":[OSD([sQuery(id+"F10.wireOp",EDGE,"E158.MirrorCS")])],"isStart":false})});
            var Q54;
            Q54=makeQuery(id+"F12.boolean.opBoolean","COPY",EDGE,{"derivedFrom":makeQuery(id+"F12.opExtrude","CAP_EDGE",EDGE,{"disambiguationData":[OSD([sQuery(id+"F10.wireOp",EDGE,"E182.trimOffspring")])],"isStart":false})});
            var Q55;
            Q55=makeQuery(id+"F12.boolean.opBoolean","COPY",EDGE,{"derivedFrom":makeQuery(id+"F12.opExtrude","CAP_EDGE",EDGE,{"disambiguationData":[OSD([sQuery(id+"F10.wireOp",EDGE,"E169.MirrorCS")])],"isStart":false})});
            var Q56;
            Q56=makeQuery(id+"F12.boolean.opBoolean","COPY",EDGE,{"derivedFrom":makeQuery(id+"F12.opExtrude","CAP_EDGE",EDGE,{"disambiguationData":[OSD([sQuery(id+"F10.wireOp",EDGE,"E184.trimOffspring")])],"isStart":false})});
            var Q57;
            Q57=makeQuery(id+"F12.boolean.opBoolean","COPY",EDGE,{"derivedFrom":makeQuery(id+"F12.opExtrude","CAP_EDGE",EDGE,{"disambiguationData":[OSD([sQuery(id+"F10.wireOp",EDGE,"E118.MirrorCS")])],"isStart":false})});
            var Q58;
            Q58=makeQuery(id+"F12.boolean.opBoolean","COPY",EDGE,{"derivedFrom":makeQuery(id+"F12.opExtrude","CAP_EDGE",EDGE,{"disambiguationData":[OSD([sQuery(id+"F10.wireOp",EDGE,"E140.MirrorCS")])],"isStart":false})});
            var Q59;
            Q59=makeQuery(id+"F12.boolean.opBoolean","COPY",EDGE,{"derivedFrom":makeQuery(id+"F12.opExtrude","CAP_EDGE",EDGE,{"disambiguationData":[OSD([sQuery(id+"F10.wireOp",EDGE,"E116.MirrorCS")])],"isStart":false})});
            var Q60;
            Q60=makeQuery(id+"F12.boolean.opBoolean","COPY",EDGE,{"derivedFrom":makeQuery(id+"F12.opExtrude","CAP_EDGE",EDGE,{"disambiguationData":[OSD([sQuery(id+"F10.wireOp",EDGE,"E124.MirrorCS")])],"isStart":false})});
            var Q61;
            Q61=makeQuery(id+"F12.boolean.opBoolean","COPY",EDGE,{"derivedFrom":makeQuery(id+"F12.opExtrude","CAP_EDGE",EDGE,{"disambiguationData":[OSD([sQuery(id+"F10.wireOp",EDGE,"E135.MirrorCS")])],"isStart":false})});
            var Q62;
            Q62=makeQuery(id+"F12.boolean.opBoolean","COPY",EDGE,{"derivedFrom":makeQuery(id+"F12.opExtrude","CAP_EDGE",EDGE,{"disambiguationData":[OSD([sQuery(id+"F10.wireOp",EDGE,"E15")])],"isStart":false})});
            var Q63;
            Q63=makeQuery(id+"F12.boolean.opBoolean","COPY",EDGE,{"derivedFrom":makeQuery(id+"F12.opExtrude","CAP_EDGE",EDGE,{"disambiguationData":[OSD([sQuery(id+"F10.wireOp",EDGE,"E38.trimOffspring")])],"isStart":false})});
            var Q64;
            Q64=makeQuery(id+"F12.boolean.opBoolean","COPY",EDGE,{"derivedFrom":makeQuery(id+"F12.opExtrude","CAP_EDGE",EDGE,{"disambiguationData":[OSD([sQuery(id+"F10.wireOp",EDGE,"E167.MirrorCS")])],"isStart":false})});
            var Q65;
            Q65=makeQuery(id+"F12.boolean.opBoolean","COPY",EDGE,{"derivedFrom":makeQuery(id+"F12.opExtrude","CAP_EDGE",EDGE,{"disambiguationData":[OSD([sQuery(id+"F10.wireOp",EDGE,"E170.MirrorCS")])],"isStart":false})});
            var Q66;
            Q66=makeQuery(id+"F12.boolean.opBoolean","COPY",EDGE,{"derivedFrom":makeQuery(id+"F12.opExtrude","CAP_EDGE",EDGE,{"disambiguationData":[OSD([sQuery(id+"F10.wireOp",EDGE,"E185.trimOffspring")])],"isStart":false})});
            var Q67;
            Q67=makeQuery(id+"F12.boolean.opBoolean","COPY",EDGE,{"derivedFrom":makeQuery(id+"F12.opExtrude","CAP_EDGE",EDGE,{"disambiguationData":[OSD([sQuery(id+"F10.wireOp",EDGE,"E183.trimOffspring")])],"isStart":false})});
            var Q68;
            Q68=makeQuery(id+"F12.boolean.opBoolean","COPY",EDGE,{"derivedFrom":makeQuery(id+"F12.opExtrude","CAP_EDGE",EDGE,{"disambiguationData":[OSD([sQuery(id+"F10.wireOp",EDGE,"E160.MirrorCS")])],"isStart":false})});
            var Q69;
            Q69=makeQuery(id+"F12.boolean.opBoolean","COPY",EDGE,{"derivedFrom":makeQuery(id+"F12.opExtrude","CAP_EDGE",EDGE,{"disambiguationData":[OSD([sQuery(id+"F10.wireOp",EDGE,"E157.MirrorCS")])],"isStart":false})});
            var Q70;
            Q70=makeQuery(id+"F12.boolean.opBoolean","COPY",EDGE,{"derivedFrom":makeQuery(id+"F12.opExtrude","CAP_EDGE",EDGE,{"disambiguationData":[OSD([sQuery(id+"F10.wireOp",EDGE,"E186.trimOffspring")])],"isStart":false})});
            var Q71;
            Q71=makeQuery(id+"F12.boolean.opBoolean","COPY",EDGE,{"derivedFrom":makeQuery(id+"F12.opExtrude","CAP_EDGE",EDGE,{"disambiguationData":[OSD([sQuery(id+"F10.wireOp",EDGE,"E113.MirrorCS")])],"isStart":false})});
            var Q72;
            Q72=makeQuery(id+"F12.boolean.opBoolean","COPY",EDGE,{"derivedFrom":makeQuery(id+"F12.opExtrude","CAP_EDGE",EDGE,{"disambiguationData":[OSD([sQuery(id+"F10.wireOp",EDGE,"E111.MirrorCS")])],"isStart":false})});
            chamfer(context, id + "F13", {"entities" : qUnion([Q0, Q1, Q2, Q3, Q4, Q5, Q6, Q7, Q8, Q9, Q10, Q11, Q12, Q13, Q14, Q15, Q16, Q17, Q18, Q19, Q20, Q21, Q22, Q23, Q24, Q25, Q26, Q27, Q28, Q29, Q30, Q31, Q32, Q33, Q34, Q35, Q36, Q37, Q38, Q39, Q40, Q41, Q42, Q43, Q44, Q45, Q46, Q47, Q48, Q49, Q50, Q51, Q52, Q53, Q54, Q55, Q56, Q57, Q58, Q59, Q60, Q61, Q62, Q63, Q64, Q65, Q66, Q67, Q68, Q69, Q70, Q71, Q72]), "width" : 2 * mm, "tangentPropagation" : true});
        }
    });
